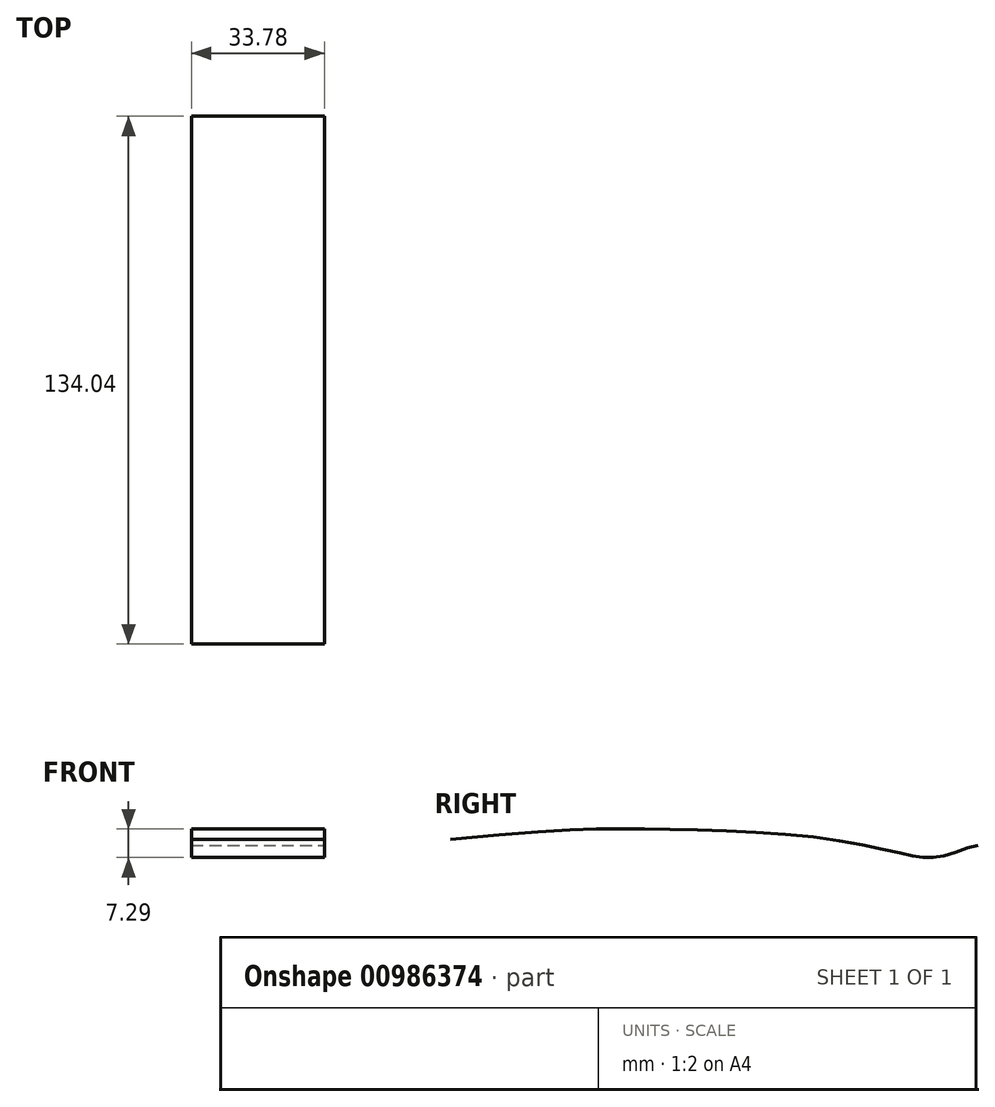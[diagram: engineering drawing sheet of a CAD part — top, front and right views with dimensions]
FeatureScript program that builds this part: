
annotation { "Feature Type Name" : "Feature", "Feature Type Description" : "" }
export const myFeature = defineFeature(function(context is Context, id is Id, definition is map)
    precondition{}
    {
        {
            var Q0;
            Q0=qCreatedBy(makeId("Right.planeOp"),FACE);
            var sketch = newSketch(context, id + "F0", { "sketchPlane" : qUnion([Q0])});
            skFitSpline(sketch, "E0", {"points": [v(71.71, 4.01) * mm, v(40.89, 4.47) * mm, v(9.57, 8.08) * mm, v(-27.1, 6.93) * mm, v(-65.63, 0) * mm], "startDerivative": vector(-125.07, 1.27) * mm, "endDerivative": vector(-145.76, -33.62) * mm});
            skFitSpline(sketch, "E1", {"points": [v(65.02, 0) * mm, v(58.3, -2.07) * mm, v(52.15, -3.05) * mm, v(46.09, -2.14) * mm, v(23.04, 2.15) * mm, v(-17.6, 4.13) * mm, v(-69.02, 1.54) * mm], "startDerivative": vector(-57.51, 0) * mm, "endDerivative": vector(-316.92, -31.97) * mm});
            skSolve(sketch);
        }
        {
            var Q0;
            Q0=sQuery(id+"F0.wireOp",EDGE,"E1");
            extrude(context, id + "F1", {"bodyType" : ToolBodyType.SURFACE, "surfaceEntities" : qUnion([Q0]), "depth" : 33.78 * mm, "offsetDistance" : 25.4 * mm});
        }
    });
